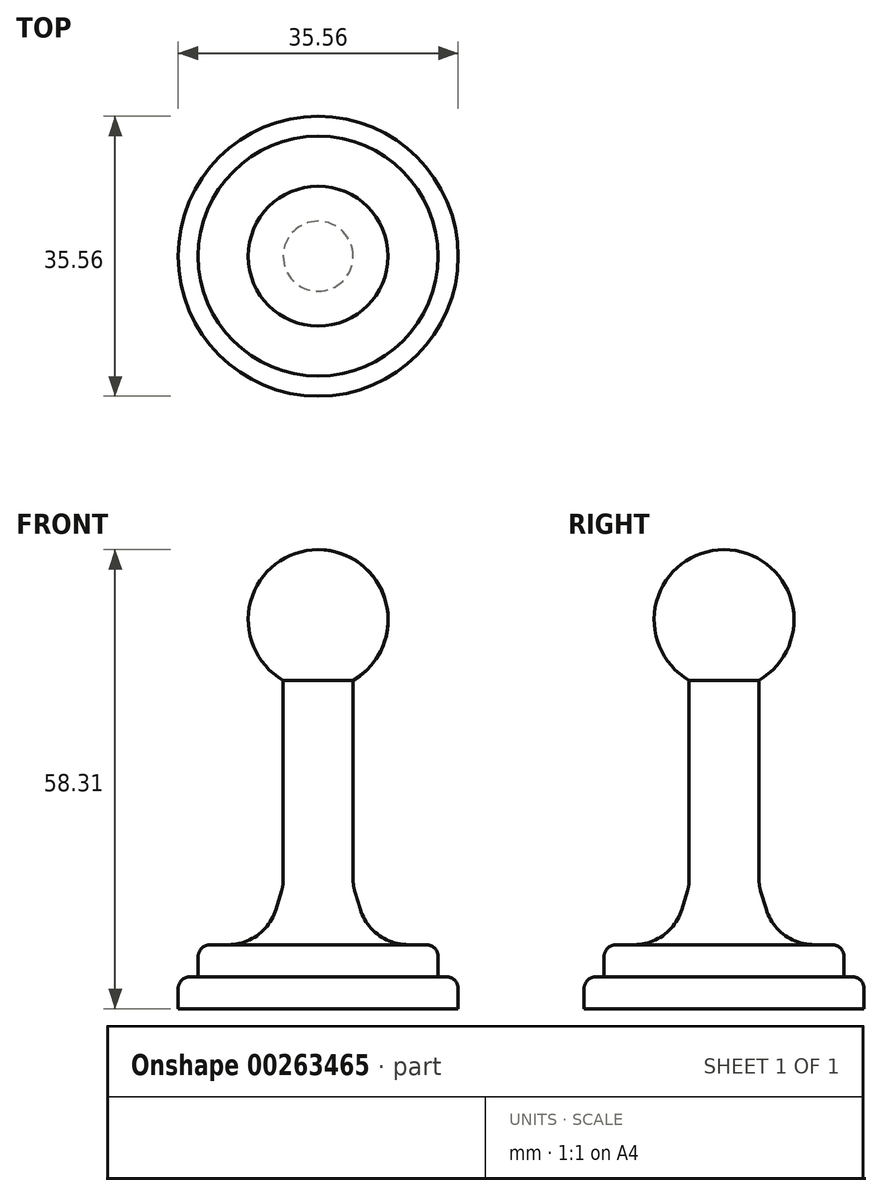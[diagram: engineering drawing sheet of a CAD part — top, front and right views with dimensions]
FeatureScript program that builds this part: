
annotation { "Feature Type Name" : "Feature", "Feature Type Description" : "" }
export const myFeature = defineFeature(function(context is Context, id is Id, definition is map)
    precondition{}
    {
        {
            var Q0;
            Q0=qCreatedBy(makeId("Front.planeOp"),FACE);
            var sketch = newSketch(context, id + "F0", { "sketchPlane" : qUnion([Q0])});
            skLineSegment(sketch, "E0", {"start": v(0, 0) * mm, "end": v(-17.78, 0) * mm});
            skLineSegment(sketch, "E1", {"start": v(-17.78, 0) * mm, "end": v(-17.78, 2.54) * mm});
            skLineSegment(sketch, "E2", {"start": v(-16.26, 4.06) * mm, "end": v(-15.24, 4.06) * mm});
            skLineSegment(sketch, "E3", {"start": v(-15.24, 4.06) * mm, "end": v(-15.24, 6.6) * mm});
            skLineSegment(sketch, "E4", {"start": v(-13.72, 8.13) * mm, "end": v(-11.43, 8.13) * mm});
            skPoint(sketch, "E4.endSnap0", {"position": v(-8.89, 0) * mm});
            skLineSegment(sketch, "E5", {"start": v(-5.35, 12.63) * mm, "end": v(-4.65, 14.96) * mm});
            skLineSegment(sketch, "E6", {"start": v(-4.44, 16.32) * mm, "end": v(-4.44, 41.72) * mm});
            skArc(sketch, "E7", {"start": v(-4.44, 41.72) * mm, "mid": v(-8.59, 51.72) * mm, "end": v(0, 58.3) * mm});
            skArc(sketch, "E8.filletArc", {"start": v(-4.65, 14.96) * mm, "mid": v(-4.5, 15.63) * mm, "end": v(-4.44, 16.32) * mm});
            skArc(sketch, "E9.filletArc", {"start": v(-11.43, 8.13) * mm, "mid": v(-7.65, 9.38) * mm, "end": v(-5.35, 12.63) * mm});
            skArc(sketch, "E10.filletArc", {"start": v(-13.72, 8.13) * mm, "mid": v(-14.8, 7.68) * mm, "end": v(-15.24, 6.6) * mm});
            skArc(sketch, "E11.filletArc", {"start": v(-16.26, 4.06) * mm, "mid": v(-17.33, 3.62) * mm, "end": v(-17.78, 2.54) * mm});
            skLineSegment(sketch, "E12", {"start": v(0, 69.52) * mm, "end": v(0, -6.3) * mm, "construction": true});
            skLineSegment(sketch, "E13", {"start": v(0, 58.3) * mm, "end": v(0, 0) * mm});
            skSolve(sketch);
        }
        {
            var Q0;
            Q0=makeQuery(id+"F0.imprint","IMPRINT",FACE,{"disambiguationData":[TD([[makeQuery(id+"F0.imprint","IMPRINT",EDGE,{"derivedFrom":sQuery(id+"F0.wireOp",EDGE,"E0")}),-1.0]])]});
            var Q1;
            Q1=sQuery(id+"F0.wireOp",EDGE,"E12");
            revolve(context, id + "F1", {"entities" : qUnion([Q0]), "axis" : qUnion([Q1]), "revolveType" : RevolveType.FULL});
        }
    });
